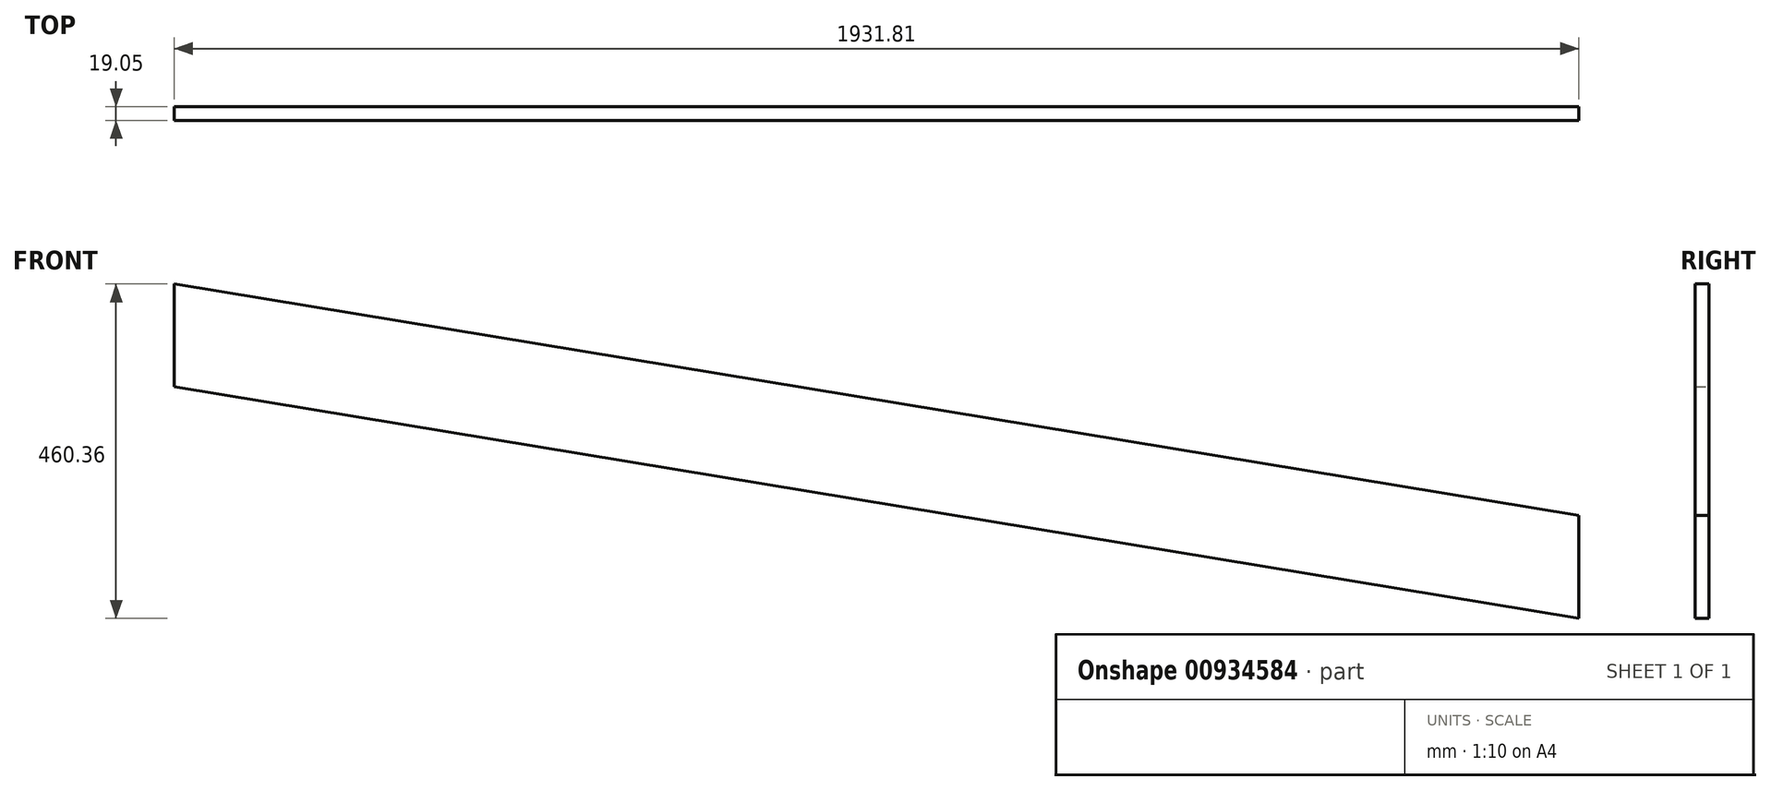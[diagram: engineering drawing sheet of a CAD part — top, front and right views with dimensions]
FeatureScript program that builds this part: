
annotation { "Feature Type Name" : "Feature", "Feature Type Description" : "" }
export const myFeature = defineFeature(function(context is Context, id is Id, definition is map)
    precondition{}
    {
        {
            var Q0;
            Q0=qCreatedBy(makeId("Front.planeOp"),FACE);
            var sketch = newSketch(context, id + "F0", { "sketchPlane" : qUnion([Q0])});
            skLineSegment(sketch, "E0.0", {"start": v(1987.74, -634.8) * mm, "end": v(3919.55, -953.57) * mm});
            skLineSegment(sketch, "E1", {"start": v(3919.55, -811.98) * mm, "end": v(3919.55, -953.57) * mm});
            skLineSegment(sketch, "E2", {"start": v(1987.74, -493.2) * mm, "end": v(1987.74, -634.8) * mm});
            skLineSegment(sketch, "E3", {"start": v(1987.74, -493.2) * mm, "end": v(3919.55, -811.98) * mm});
            skSolve(sketch);
        }
        {
            var Q0;
            Q0=makeQuery(id+"F0.imprint","IMPRINT",FACE,{"disambiguationData":[TD([[makeQuery(id+"F0.imprint","IMPRINT",EDGE,{"derivedFrom":sQuery(id+"F0.wireOp",EDGE,"E0.0")}),1.0]])]});
            extrude(context, id + "F1", {"entities" : qUnion([Q0]), "depth" : 19.05 * mm, "offsetDistance" : 25.4 * mm});
        }
    });
